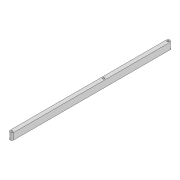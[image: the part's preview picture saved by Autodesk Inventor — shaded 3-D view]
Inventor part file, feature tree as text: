
AUTODESK INVENTOR PART (.ipt)
format: ipt  version: 2022 (Build 260153000, 153)  size: 88,064 bytes
history: native  units: mm
features: extrude x1, sketch x1
ambient origin geometry x8: Origin, YZ Plane, XZ Plane, XY Plane, X Axis, Y Axis, Z Axis, Center Point
bodies: Solid1 (feature_tree)
feature tree (2):
  extrude  "Extrusion1"  Depth=240.109mm
  sketch  "Sketch1"  dims[d0=6.0mm d1=240.109mm d2=3.0mm d3=3.0mm d4=10.0mm d5=0.0mm d6=3.0mm d7=141.04mm]
